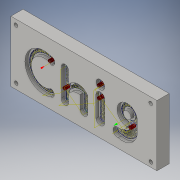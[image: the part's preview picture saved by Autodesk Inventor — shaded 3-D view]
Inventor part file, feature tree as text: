
AUTODESK INVENTOR PART (.ipt)
format: ipt  version: 2016 (Build 200138000, 138)  size: 387,072 bytes
history: native  units: in
note: dims shown in document units (in); Inventor stores cm internally (conversion verified against a paired STEP export)
features: hole x4, sketch x2, extrude x1, emboss x1
ambient origin geometry x8: Origin, YZ Plane, XZ Plane, XY Plane, X Axis, Y Axis, Z Axis, Center Point
bodies: Solid1 (feature_tree)
feature tree (8):
  extrude  "Extrusion1"  Depth=12.0in
  emboss  "Emboss1"
  hole  "Hole1"  [1 undecoded]
  hole  "Hole2"  [1 undecoded]
  hole  "Hole3"  [1 undecoded]
  hole  "Hole4"  [1 undecoded]
  sketch  "Sketch1"  dims[d0=5.0in d1=12.0in]
  sketch  "Sketch2"  dims[d2=1.0in d3=0.0in d4=0.25in d5=0.0in d44=1.0in d45=1.0in d8=0.3in d9=0.75in d10=0.375in d11=0.25in d12=0.5635in d13=1.0in d14=0.8108in d50=1.0in d51=1.0in d17=0.3in d18=0.75in d19=0.375in d20=0.25in d21=0.5635in d22=1.0in d23=0.8108in d46=1.0in d47=1.0in d26=0.3in d27=0.75in d28=0.375in d29=0.25in d30=0.5635in d31=1.0in d32=0.8108in d48=1.0in d49=1.0in d35=0.3in d36=0.75in d37=0.375in d38=0.25in d39=0.5635in d40=1.0in d41=0.8108in d42=0.52in d43=0.52in]
note: 4 required parameter values undecoded (feature->parameter linkage not recoverable at this tier; creation-order binding heuristic only, values carry confidence <= 0.55)
